# Revit family: Specialty_Equipment-Fiberglass_Planter-Planters_Unlimited-Balboa-Low Bowl
name_source: partatom
category: Specialty Equipment
units: mm (PartAtom-declared; Revit-internal decimal feet)

## family parameters
Always vertical = Yes
Cut with Voids When Loaded = No
Enable Cutting in Views = No
Maintain Annotation Orientation = No
OmniClass Number = 23.40.05.21.17
OmniClass Title = Planters
Part Type = Normal
Room Calculation Point = No
Round Connector Dimension = Use Diameter
Shared = No
Work Plane-Based = No

## types (4) — shared parameters
Assembly Code = G2050600
CD_Finish = Plastic-Fiberglass-Carlsbad-Semi_Gloss-Charcoal
CD_Microsite = https://www.caddetails.com
CD_Product Page URL = https://www.plantersunlimited.com
CD_Specification = https://www.plantersunlimited.com
Default Elevation = 0.0"
Description = Balboa Low Bowl Planter
Manufacturer = Planters Unlimited
Model = Balboa Low Bowl Series Planter
Type Comments = Square Planter
URL = https://www.plantersunlimited.com

## per-type parameters (varying)
| type | CD_Base Dia | CD_Diameter | CD_Height | CD_Lip Width | CD_Pad Spacing | CD_Top Lip |
| 24"Dia x 8"H | 12.0" | 24.0" | 8.0" | 20.5" | 4.8" | 6.0" |
| 30"Dia x 11"H | 15.0" | 30.0" | 11.0" | 26.5" | 6.0" | 7.5" |
| 36"Dia x 13"H | 18.0" | 36.0" | 13.0" | 32.5" | 7.2" | 9.0" |
| 42"Dia x 15"H | 21.0" | 42.0" | 15.0" | 38.5" | 8.4" | 10.5" |

## geometry (parser evidence)
native form markers: Sweep x4
no freeform markers — native parametric forms only
